# Revit family: Urinal-Wall_Mount-KOHLER-Tend-K-20713IN-1
name_source: partatom
category: Plumbing Fixtures
units: mm (PartAtom-declared; Revit-internal decimal feet)

## family parameters
Cut with Voids When Loaded = No
Host = Face
OmniClass Number = 23.31.21.00
OmniClass Title = Urinals
Part Type = Normal
Room Calculation Point = No
Round Connector Dimension = Use Diameter
Shared = No

## types (3) — shared parameters
ADA Compliant = Yes
Assembly Code = D2010200
CW Connection = Yes
Cold Water Inlet = Cold Water Inlet
Date Modified = 05/19/2024
Default Elevation = 0"
Description = Urinal, Rear Spud
Drain Included = No
Flow Rate = 0 GPM
Flush Rate- GPF = 1 GPF
Flush Rate- LPF = 3.8 LPF
HW Connection = No
Height = 21 5/8"
Hot Water Inlet = Hot Water Inlet
Length = 14 7/8"
Manufacturer = Kohler Co.
Master Format 2014 = 22 41 13.16
Master Format 2014 Name = Residential Urinals
Material = Vitreous China
Pressure = 0.00 psi
Product Name = Tend
URL = https://www.kohler.co.in
Vent Connection = No
Waste Connection = Yes
Waste Water Outlet = Waste Water Outlet
WaterSense Certified = No
Width = 13"

## per-type parameters (varying)
| type | Finish | Model | Product Documentation Link | Product Page URL | Type |
| 0-White | Kohler-Vitreous_China-0-White | K-20713IN-ER-0 | https://techcomm.kohler.com | https://www.kohler.co.in | 1 |
| 7-Black Black | Kohler-Vitreous_China-7-Black_Black | K-20713IN-ER-7 |  |  | 2 |
| 96-Biscuit | Kohler-Vitreous_China-96-Biscuit | K-20713IN-ER-96 |  |  | 3 |

## geometry (parser evidence)
native form markers: Sweep x4
no freeform markers — native parametric forms only
